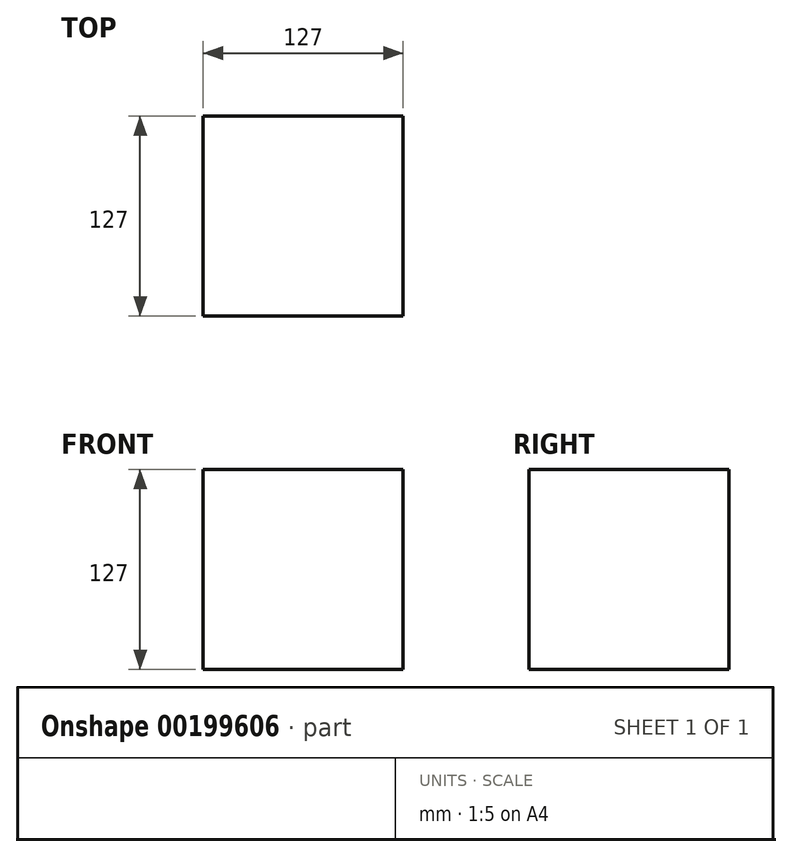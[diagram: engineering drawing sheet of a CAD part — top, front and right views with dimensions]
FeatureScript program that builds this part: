
annotation { "Feature Type Name" : "Feature", "Feature Type Description" : "" }
export const myFeature = defineFeature(function(context is Context, id is Id, definition is map)
    precondition{}
    {
        {
            var Q0;
            Q0=qCreatedBy(makeId("Top.planeOp"),FACE);
            var sketch = newSketch(context, id + "F0", { "sketchPlane" : qUnion([Q0])});
            skLineSegment(sketch, "E0.bottom", {"start": v(-43.2, 24.44) * mm, "end": v(0, 24.44) * mm});
            skLineSegment(sketch, "E0.top", {"start": v(-43.2, 0) * mm, "end": v(0, 0) * mm});
            skLineSegment(sketch, "E0.left", {"start": v(-43.2, 24.44) * mm, "end": v(-43.2, 0) * mm});
            skLineSegment(sketch, "E0.right", {"start": v(0, 24.44) * mm, "end": v(0, 0) * mm});
            skLineSegment(sketch, "E1.bottom", {"start": v(-97.94, 93.52) * mm, "end": v(29.06, 93.52) * mm});
            skLineSegment(sketch, "E1.top", {"start": v(-97.94, -33.48) * mm, "end": v(29.06, -33.48) * mm});
            skLineSegment(sketch, "E1.left", {"start": v(-97.94, 93.52) * mm, "end": v(-97.94, -33.48) * mm});
            skLineSegment(sketch, "E1.right", {"start": v(29.06, 93.52) * mm, "end": v(29.06, -33.48) * mm});
            skSolve(sketch);
        }
        {
            var Q0;
            Q0=makeQuery(id+"F0.imprint","IMPRINT",FACE,{"disambiguationData":[TD([[makeQuery(id+"F0.imprint","IMPRINT",EDGE,{"derivedFrom":sQuery(id+"F0.wireOp",EDGE,"E0.bottom")}),1.0]])]});
            var Q1;
            Q1=makeQuery(id+"F0.imprint","IMPRINT",FACE,{"disambiguationData":[TD([[makeQuery(id+"F0.imprint","IMPRINT",EDGE,{"derivedFrom":sQuery(id+"F0.wireOp",EDGE,"E0.bottom")}),-1.0]])]});
            extrude(context, id + "F1", {"entities" : qUnion([Q0, Q1]), "depth" : 127 * mm});
        }
    });
